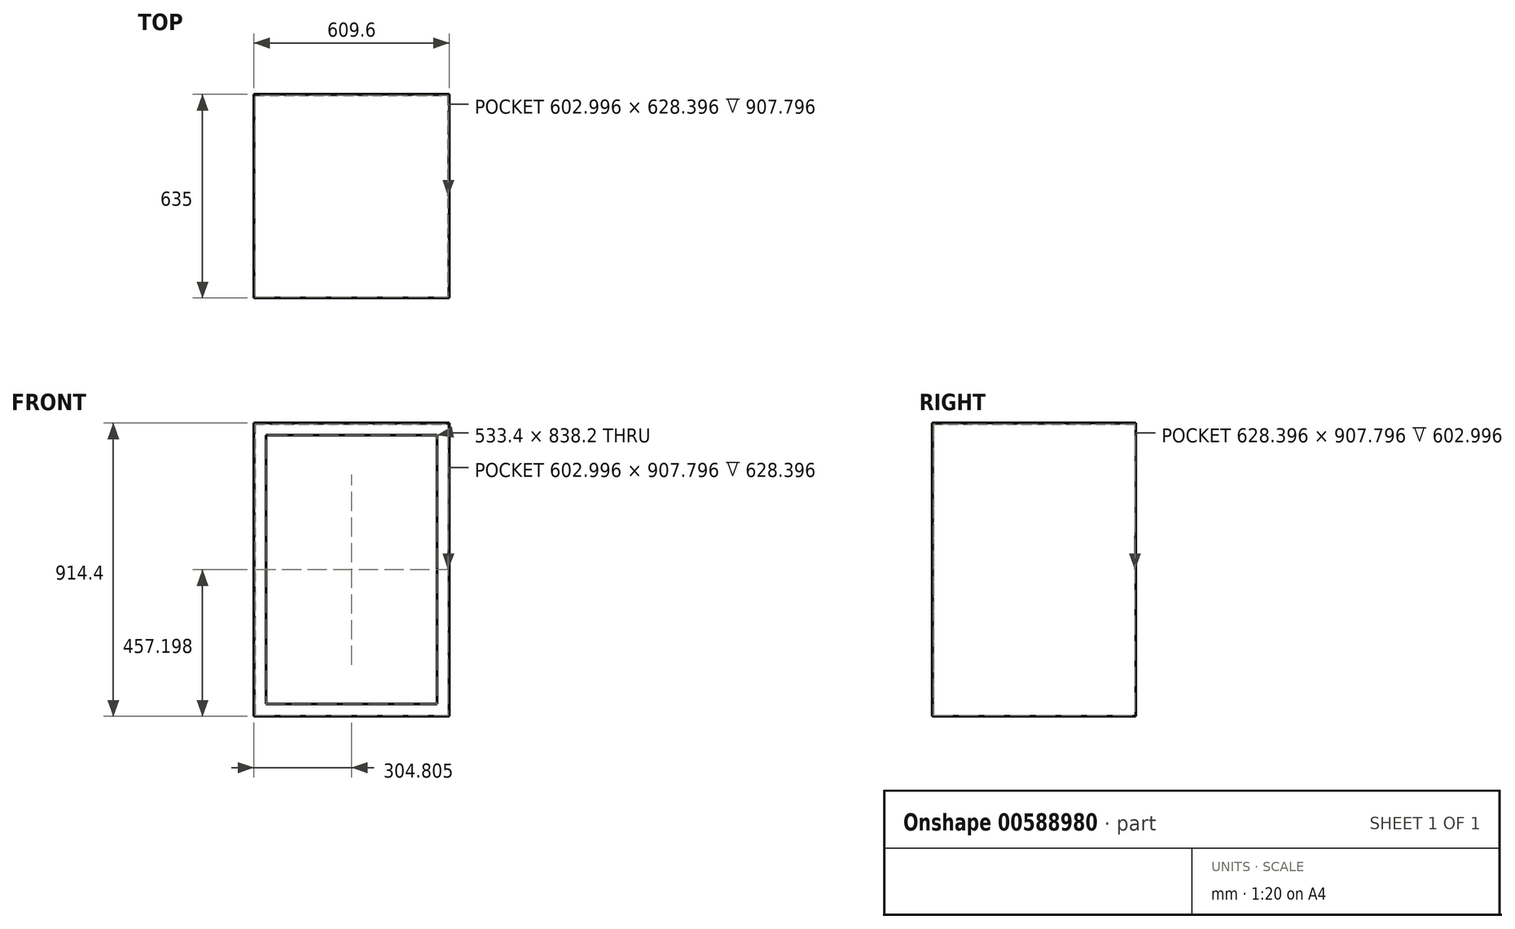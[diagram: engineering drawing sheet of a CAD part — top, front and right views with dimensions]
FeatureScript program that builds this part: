
annotation { "Feature Type Name" : "Feature", "Feature Type Description" : "" }
export const myFeature = defineFeature(function(context is Context, id is Id, definition is map)
    precondition{}
    {
        {
            var Q0;
            Q0=qCreatedBy(makeId("Front.planeOp"),FACE);
            var sketch = newSketch(context, id + "F0", { "sketchPlane" : qUnion([Q0])});
            skLineSegment(sketch, "E0.bottom", {"start": v(-431.95, 452.54) * mm, "end": v(177.65, 452.54) * mm});
            skLineSegment(sketch, "E0.top", {"start": v(-431.95, -461.86) * mm, "end": v(177.65, -461.86) * mm});
            skLineSegment(sketch, "E0.left", {"start": v(-431.95, 452.54) * mm, "end": v(-431.95, -461.86) * mm});
            skLineSegment(sketch, "E0.right", {"start": v(177.65, 452.54) * mm, "end": v(177.65, -461.86) * mm});
            skSolve(sketch);
        }
        {
            var Q0;
            Q0=makeQuery(id+"F0.imprint","IMPRINT",FACE,{"disambiguationData":[TD([[makeQuery(id+"F0.imprint","IMPRINT",EDGE,{"derivedFrom":sQuery(id+"F0.wireOp",EDGE,"E0.bottom")}),-1.0]])]});
            extrude(context, id + "F1", {"entities" : qUnion([Q0]), "depth" : 609.6 * mm, "offsetDistance" : 25.4 * mm});
        }
        {
            var Q0;
            Q0=makeQuery(id+"F1.opExtrude","CAP_FACE",FACE,{"disambiguationData":[OSD([sQuery(id+"F0.wireOp",EDGE,"E0.bottom"),sQuery(id+"F0.wireOp",EDGE,"E0.top"),sQuery(id+"F0.wireOp",EDGE,"E0.left"),sQuery(id+"F0.wireOp",EDGE,"E0.right")])],"isStart":false});
            extrude(context, id + "F2", {"entities" : qUnion([Q0]), "operationType" : NewBodyOperationType.ADD, "depth" : 25.4 * mm, "offsetDistance" : 25.4 * mm});
        }
        {
            var Q0;
            Q0=makeQuery(id+"F2.opExtrude","CAP_FACE",FACE,{"disambiguationData":[OSD([sQuery(id+"F0.wireOp",EDGE,"E0.bottom"),sQuery(id+"F0.wireOp",EDGE,"E0.top"),sQuery(id+"F0.wireOp",EDGE,"E0.left"),sQuery(id+"F0.wireOp",EDGE,"E0.right")])],"isStart":false});
            var Q1;
            Q1=makeQuery(id+"F1.opExtrude","SWEPT_BODY",BODY,{"disambiguationData":[OSD([sQuery(id+"F0.wireOp",EDGE,"E0.bottom"),sQuery(id+"F0.wireOp",EDGE,"E0.top"),sQuery(id+"F0.wireOp",EDGE,"E0.left"),sQuery(id+"F0.wireOp",EDGE,"E0.right")])]});
            shell(context, id + "F3", {"isHollow" : true, "entities" : qUnion([Q0]), "parts" : qUnion([Q1]), "thickness" : 3.3 * mm});
        }
        {
            var Q0;
            Q0=makeQuery(id+"F2.opExtrude","CAP_FACE",FACE,{"disambiguationData":[OSD([sQuery(id+"F0.wireOp",EDGE,"E0.bottom"),sQuery(id+"F0.wireOp",EDGE,"E0.top"),sQuery(id+"F0.wireOp",EDGE,"E0.left"),sQuery(id+"F0.wireOp",EDGE,"E0.right")])],"isStart":false});
            var sketch = newSketch(context, id + "F4", { "sketchPlane" : qUnion([Q0])});
            skLineSegment(sketch, "E1.bottom", {"start": v(-393.85, 414.44) * mm, "end": v(139.55, 414.44) * mm});
            skLineSegment(sketch, "E1.top", {"start": v(-393.85, -423.76) * mm, "end": v(139.55, -423.76) * mm});
            skLineSegment(sketch, "E1.left", {"start": v(-393.85, 414.44) * mm, "end": v(-393.85, -423.76) * mm});
            skLineSegment(sketch, "E1.right", {"start": v(139.55, 414.44) * mm, "end": v(139.55, -423.76) * mm});
            skSolve(sketch);
        }
        {
            var Q0;
            Q0 = qSketchRegion(id + "F4", true);
            extrude(context, id + "F5", {"entities" : qUnion([Q0]), "operationType" : NewBodyOperationType.REMOVE, "oppositeDirection" : true, "depth" : 584.2 * mm, "offsetDistance" : 25.4 * mm});
        }
    });
